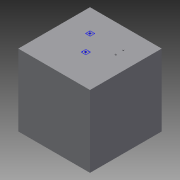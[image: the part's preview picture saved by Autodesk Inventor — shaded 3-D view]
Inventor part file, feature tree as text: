
AUTODESK INVENTOR PART (.ipt)
format: ipt  version: 2014 (Build 180170000, 170)  size: 292,864 bytes
history: native  units: mm
features: other x50, sketch x5, extrude x1
ambient origin geometry x8: Origin, YZ Plane, XZ Plane, XY Plane, X Axis, Y Axis, Z Axis, Center Point
bodies: 实体1 (feature_tree)
feature tree (56):
  extrude  "拉伸1"  TaperAngle=0.0deg  [1 undecoded]
  other  "UCS1"
  other  "UCS2"
  other  "UCS3"
  other  "UCS4"
  other  "UCS5"
  other  "UCS6"
  other  "Footprint1"
  other  "Footprint2"
  sketch  "草图1"  dims[d0=1000.0mm d1=0.0mm]
  other  "UCS1: YZ 平面"
  other  "UCS1: XZ 平面"
  other  "UCS1: XY 平面"
  other  "UCS1: X 轴"
  other  "UCS1: Y 轴"
  other  "UCS1: Z 轴"
  other  "UCS1: 原点"
  other  "UCS2: YZ 平面"
  other  "UCS2: XZ 平面"
  other  "UCS2: XY 平面"
  other  "UCS2: X 轴"
  other  "UCS2: Y 轴"
  other  "UCS2: Z 轴"
  other  "UCS2: 原点"
  other  "UCS3: YZ 平面"
  other  "UCS3: XZ 平面"
  other  "UCS3: XY 平面"
  other  "UCS3: X 轴"
  other  "UCS3: Y 轴"
  other  "UCS3: Z 轴"
  other  "UCS3: 原点"
  other  "UCS4: YZ 平面"
  other  "UCS4: XZ 平面"
  other  "UCS4: XY 平面"
  other  "UCS4: X 轴"
  other  "UCS4: Y 轴"
  other  "UCS4: Z 轴"
  other  "UCS4: 原点"
  other  "UCS5: YZ 平面"
  other  "UCS5: XZ 平面"
  other  "UCS5: XY 平面"
  other  "UCS5: X 轴"
  other  "UCS5: Y 轴"
  other  "UCS5: Z 轴"
  other  "UCS5: 原点"
  other  "UCS6: YZ 平面"
  other  "UCS6: XZ 平面"
  other  "UCS6: XY 平面"
  other  "UCS6: X 轴"
  other  "UCS6: Y 轴"
  other  "UCS6: Z 轴"
  other  "UCS6: 原点"
  sketch  "草图2"  dims[d2=0.0mm d3=0.0mm d4=0.0mm d5=0.0mm d6=0.0mm d7=0.0mm]
  sketch  "草图3"  dims[d8=0.0mm d9=0.0mm d10=0.0mm d11=0.0mm d12=0.0mm d13=0.0mm]
  sketch  "草图8"  dims[d14=0.0mm d15=0.0mm d16=0.0mm d17=0.0mm d18=0.0mm d19=0.0mm]
  sketch  "草图10"  dims[d20=0.0mm d21=0.0mm d22=0.0mm d23=0.0mm d24=0.0mm d25=0.0mm d26=0.0mm d27=0.0mm d28=0.0mm d29=0.0mm d30=0.0mm d31=0.0mm d32=0.0mm d33=0.0mm d34=0.0mm d35=0.0mm d36=0.0mm d37=0.0mm d38=0.0mm d42=0.0mm d46=0.0mm d52=0.0mm d58=0.0mm d64=0.0mm]
note: 1 required parameter value undecoded (feature->parameter linkage not recoverable at this tier; creation-order binding heuristic only, values carry confidence <= 0.55)
